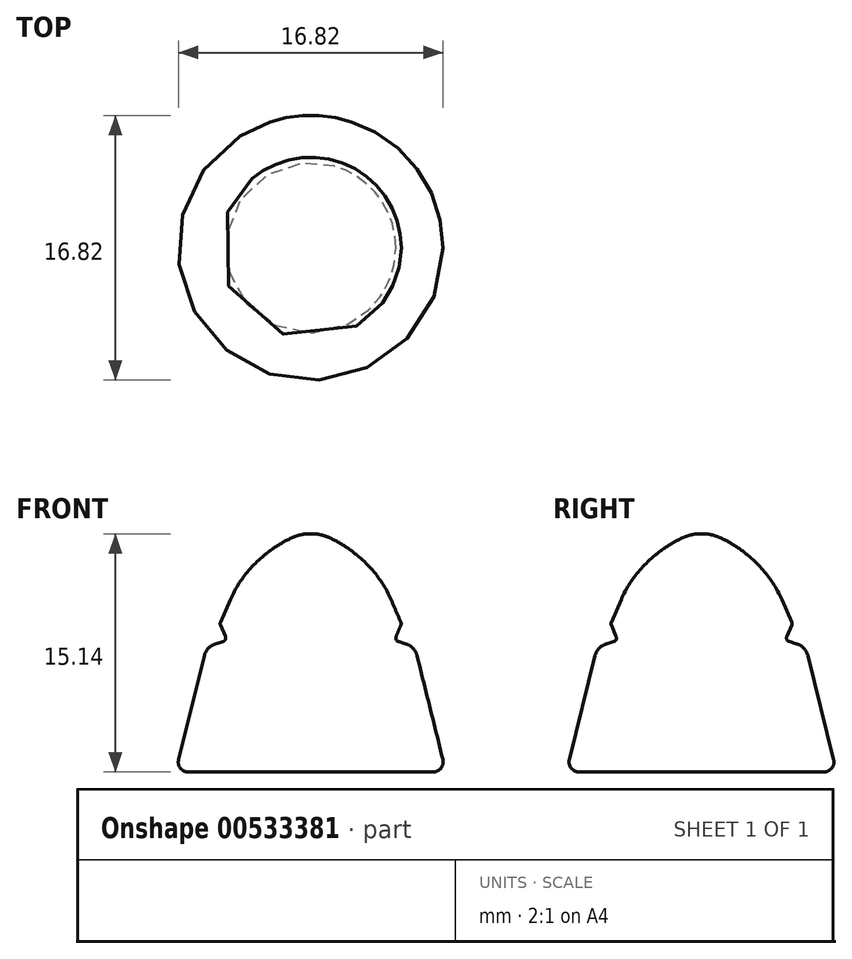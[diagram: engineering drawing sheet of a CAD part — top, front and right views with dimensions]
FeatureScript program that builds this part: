
annotation { "Feature Type Name" : "Feature", "Feature Type Description" : "" }
export const myFeature = defineFeature(function(context is Context, id is Id, definition is map)
    precondition{}
    {
        {
            var Q0;
            Q0=qCreatedBy(makeId("Front.planeOp"),FACE);
            var sketch = newSketch(context, id + "F0", { "sketchPlane" : qUnion([Q0])});
            skLineSegment(sketch, "E0", {"start": v(0, 0) * mm, "end": v(-8.6, 0) * mm});
            skLineSegment(sketch, "E1", {"start": v(-8.6, 0) * mm, "end": v(-6.61, 7.98) * mm});
            skLineSegment(sketch, "E2", {"start": v(-6.61, 7.98) * mm, "end": v(-5.32, 8.36) * mm});
            skLineSegment(sketch, "E3", {"start": v(-5.32, 8.36) * mm, "end": v(-5.77, 9.43) * mm});
            skLineSegment(sketch, "E4", {"start": v(-5.77, 9.43) * mm, "end": v(-4.4, 12.55) * mm});
            skLineSegment(sketch, "E5", {"start": v(-4.4, 12.55) * mm, "end": v(-2.04, 14.53) * mm});
            skLineSegment(sketch, "E6", {"start": v(-2.04, 14.53) * mm, "end": v(-0.6, 15.14) * mm});
            skLineSegment(sketch, "E7", {"start": v(-0.6, 15.14) * mm, "end": v(0, 15.14) * mm});
            skLineSegment(sketch, "E8", {"start": v(0, 15.14) * mm, "end": v(0, 0) * mm});
            skSolve(sketch);
        }
        {
            var Q0;
            Q0=makeQuery(id+"F0.imprint","IMPRINT",FACE,{"disambiguationData":[TD([[makeQuery(id+"F0.imprint","IMPRINT",EDGE,{"derivedFrom":sQuery(id+"F0.wireOp",EDGE,"E0")}),-1.0]])]});
            var Q1;
            Q1=sQuery(id+"F0.wireOp",EDGE,"E8");
            revolve(context, id + "F1", {"entities" : qUnion([Q0]), "axis" : qUnion([Q1]), "revolveType" : RevolveType.FULL});
        }
        {
            var Q0;
            Q0=makeQuery(id+"F1.opRevolve","SWEPT_FACE",FACE,{"disambiguationData":[OSD([sQuery(id+"F0.wireOp",EDGE,"E3")])]});
            fillet(context, id + "F2", {"entities" : qUnion([Q0]), "radius" : 0.24 * mm, "tangentPropagation" : true, "allowEdgeOverflow" : false});
        }
        {
            var Q0;
            Q0=makeQuery(id+"F1.opRevolve","SWEPT_EDGE",EDGE,{"disambiguationData":[OSD([sQuery(id+"F0.wireOp",EDGE,"E1"),sQuery(id+"F0.wireOp",EDGE,"E2")])]});
            fillet(context, id + "F3", {"entities" : qUnion([Q0]), "radius" : 1.05 * mm, "tangentPropagation" : true, "allowEdgeOverflow" : false});
        }
        {
            var Q0;
            Q0=makeQuery(id+"F1.opRevolve","SWEPT_FACE",FACE,{"disambiguationData":[OSD([sQuery(id+"F0.wireOp",EDGE,"E5")])]});
            fillet(context, id + "F4", {"entities" : qUnion([Q0]), "radius" : 7.42 * mm, "tangentPropagation" : true, "allowEdgeOverflow" : false});
        }
        {
            var Q0;
            Q0=makeQuery(id+"F1.opRevolve","SWEPT_FACE",FACE,{"disambiguationData":[OSD([sQuery(id+"F0.wireOp",EDGE,"E6")])]});
            fillet(context, id + "F5", {"entities" : qUnion([Q0]), "radius" : 2.72 * mm, "tangentPropagation" : true, "allowEdgeOverflow" : false});
        }
        {
            var Q0;
            Q0=makeQuery(id+"F1.opRevolve","SWEPT_EDGE",EDGE,{"disambiguationData":[OSD([sQuery(id+"F0.wireOp",EDGE,"E0"),sQuery(id+"F0.wireOp",EDGE,"E1")])]});
            fillet(context, id + "F6", {"entities" : qUnion([Q0]), "radius" : 0.64 * mm, "tangentPropagation" : true, "allowEdgeOverflow" : false});
        }
    });
